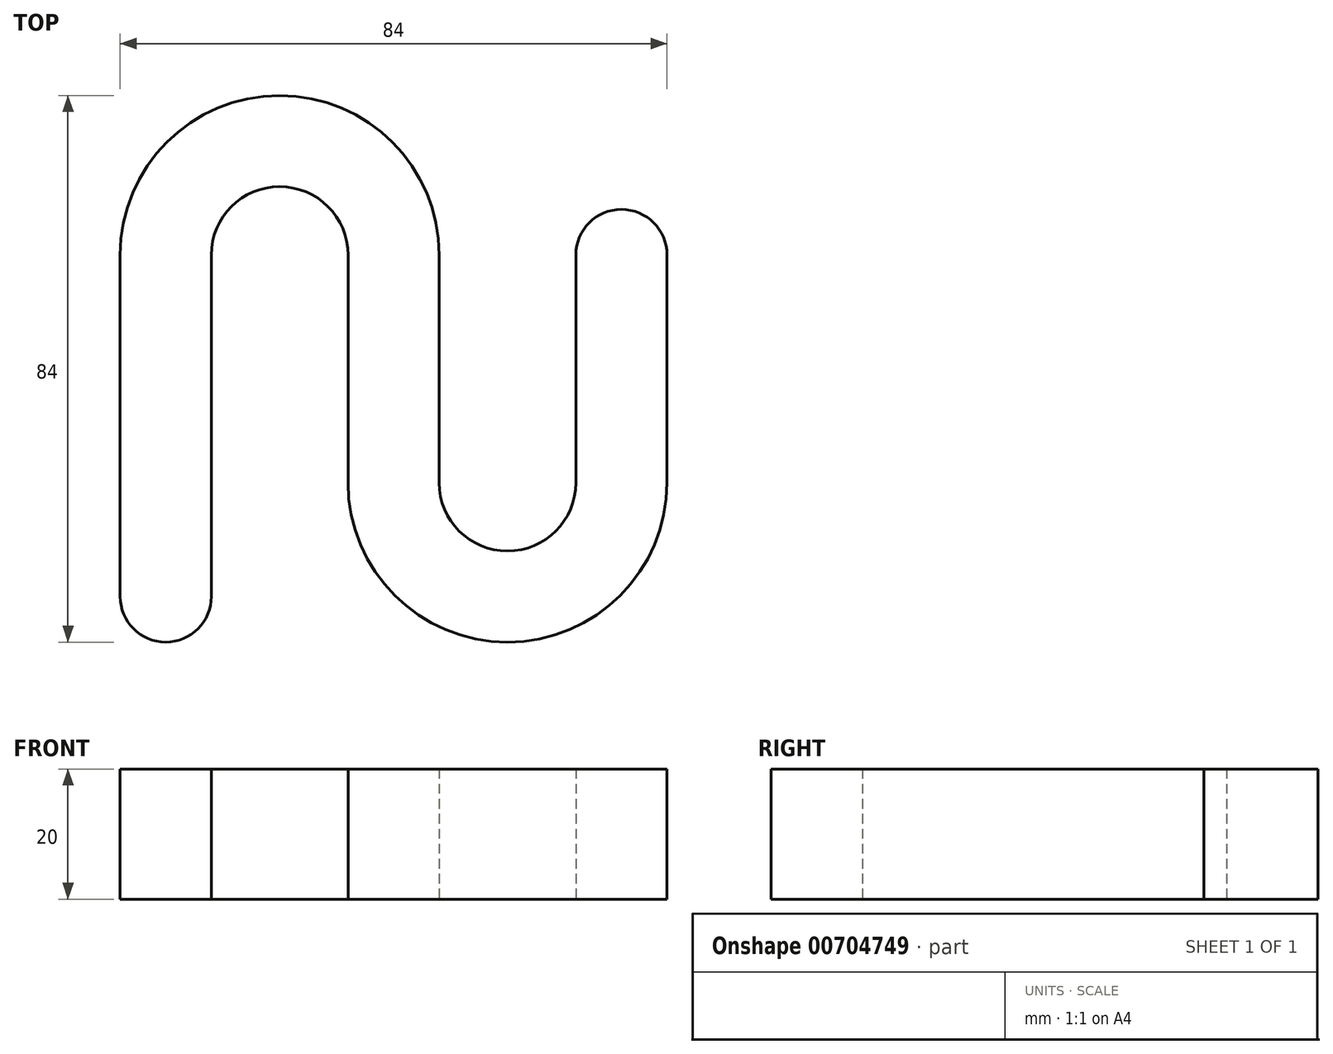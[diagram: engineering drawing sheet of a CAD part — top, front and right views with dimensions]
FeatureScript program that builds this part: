
annotation { "Feature Type Name" : "Feature", "Feature Type Description" : "" }
export const myFeature = defineFeature(function(context is Context, id is Id, definition is map)
    precondition{}
    {
        {
            var Q0;
            Q0=qCreatedBy(makeId("Top.planeOp"),FACE);
            var sketch = newSketch(context, id + "F0", { "sketchPlane" : qUnion([Q0])});
            skPoint(sketch, "E0.middle", {"position": v(0, 0) * mm});
            skLineSegment(sketch, "E1", {"start": v(-35, -17.5) * mm, "end": v(-35, 17.5) * mm, "construction": true});
            skArc(sketch, "E2", {"start": v(0, 17.5) * mm, "mid": v(-17.5, 35) * mm, "end": v(-35, 17.5) * mm, "construction": true});
            skLineSegment(sketch, "E3", {"start": v(0, 17.5) * mm, "end": v(0, -17.5) * mm, "construction": true});
            skArc(sketch, "E4", {"start": v(0, -17.5) * mm, "mid": v(17.5, -35) * mm, "end": v(35, -17.5) * mm, "construction": true});
            skLineSegment(sketch, "E5", {"start": v(35, -17.5) * mm, "end": v(35, 17.5) * mm, "construction": true});
            skLineSegment(sketch, "E6", {"start": v(17.5, -35) * mm, "end": v(-35, -35) * mm, "construction": true});
            skLineSegment(sketch, "E7", {"start": v(-35, -17.5) * mm, "end": v(-35, -35) * mm, "construction": true});
            skLineSegment(sketch, "E8", {"start": v(35, 17.5) * mm, "end": v(35, 35) * mm, "construction": true});
            skArc(sketch, "E9.0.startCap", {"start": v(-42, -17.5) * mm, "mid": v(-35, -10.5) * mm, "end": v(-28, -17.5) * mm, "construction": true});
            skArc(sketch, "E9.0.endCap", {"start": v(-28, -35) * mm, "mid": v(-35, -42) * mm, "end": v(-42, -35) * mm});
            skLineSegment(sketch, "E9.0.left", {"start": v(-28, -17.5) * mm, "end": v(-28, -35) * mm});
            skLineSegment(sketch, "E9.0.right", {"start": v(-42, -17.5) * mm, "end": v(-42, -35) * mm});
            skArc(sketch, "E9.1.startCap", {"start": v(-28, -17.5) * mm, "mid": v(-35, -24.5) * mm, "end": v(-42, -17.5) * mm, "construction": true});
            skArc(sketch, "E9.1.endCap", {"start": v(-42, 17.5) * mm, "mid": v(-35, 24.5) * mm, "end": v(-28, 17.5) * mm, "construction": true});
            skLineSegment(sketch, "E9.1.left", {"start": v(-42, -17.5) * mm, "end": v(-42, 17.5) * mm});
            skLineSegment(sketch, "E9.1.right", {"start": v(-28, -17.5) * mm, "end": v(-28, 17.5) * mm});
            skArc(sketch, "E9.2.startCap", {"start": v(7, 17.5) * mm, "mid": v(0, 10.5) * mm, "end": v(-7, 17.5) * mm, "construction": true});
            skArc(sketch, "E9.2.endCap", {"start": v(-28, 17.5) * mm, "mid": v(-35, 10.5) * mm, "end": v(-42, 17.5) * mm, "construction": true});
            skArc(sketch, "E9.2.left", {"start": v(-7, 17.5) * mm, "mid": v(-17.5, 28) * mm, "end": v(-28, 17.5) * mm});
            skArc(sketch, "E9.2.right", {"start": v(7, 17.5) * mm, "mid": v(-17.5, 42) * mm, "end": v(-42, 17.5) * mm});
            skArc(sketch, "E9.3.startCap", {"start": v(-7, 17.5) * mm, "mid": v(0, 24.5) * mm, "end": v(7, 17.5) * mm, "construction": true});
            skArc(sketch, "E9.3.endCap", {"start": v(7, -17.5) * mm, "mid": v(0, -24.5) * mm, "end": v(-7, -17.5) * mm, "construction": true});
            skLineSegment(sketch, "E9.3.left", {"start": v(7, 17.5) * mm, "end": v(7, -17.5) * mm});
            skLineSegment(sketch, "E9.3.right", {"start": v(-7, 17.5) * mm, "end": v(-7, -17.5) * mm});
            skArc(sketch, "E9.4.startCap", {"start": v(-7, -17.5) * mm, "mid": v(0, -10.5) * mm, "end": v(7, -17.5) * mm, "construction": true});
            skArc(sketch, "E9.4.endCap", {"start": v(28, -17.5) * mm, "mid": v(35, -10.5) * mm, "end": v(42, -17.5) * mm, "construction": true});
            skArc(sketch, "E9.4.left", {"start": v(7, -17.5) * mm, "mid": v(17.5, -28) * mm, "end": v(28, -17.5) * mm});
            skArc(sketch, "E9.4.right", {"start": v(-7, -17.5) * mm, "mid": v(17.5, -42) * mm, "end": v(42, -17.5) * mm});
            skArc(sketch, "E9.5.startCap", {"start": v(42, -17.5) * mm, "mid": v(35, -24.5) * mm, "end": v(28, -17.5) * mm, "construction": true});
            skArc(sketch, "E9.5.endCap", {"start": v(28, 17.5) * mm, "mid": v(35, 24.5) * mm, "end": v(42, 17.5) * mm});
            skLineSegment(sketch, "E9.5.left", {"start": v(28, -17.5) * mm, "end": v(28, 17.5) * mm});
            skLineSegment(sketch, "E9.5.right", {"start": v(42, -17.5) * mm, "end": v(42, 17.5) * mm});
            skCircle(sketch, "E10", {"center": v(35, 35) * mm, "radius": 7 * mm});
            skLineSegment(sketch, "E11.bottom", {"start": v(50, 50) * mm, "end": v(-50, 50) * mm});
            skLineSegment(sketch, "E11.top", {"start": v(50, -50) * mm, "end": v(-50, -50) * mm});
            skLineSegment(sketch, "E11.left", {"start": v(50, 50) * mm, "end": v(50, -50) * mm});
            skLineSegment(sketch, "E11.right", {"start": v(-50, 50) * mm, "end": v(-50, -50) * mm});
            skSolve(sketch);
        }
        {
            var Q0;
            Q0=makeQuery(id+"F0.imprint","IMPRINT",FACE,{"disambiguationData":[TD([[makeQuery(id+"F0.imprint","IMPRINT",EDGE,{"derivedFrom":sQuery(id+"F0.wireOp",EDGE,"E9.0.endCap")}),1.0]])]});
            extrude(context, id + "F1", {"entities" : qUnion([Q0]), "depth" : 20 * mm, "offsetDistance" : 25 * mm});
        }
    });
